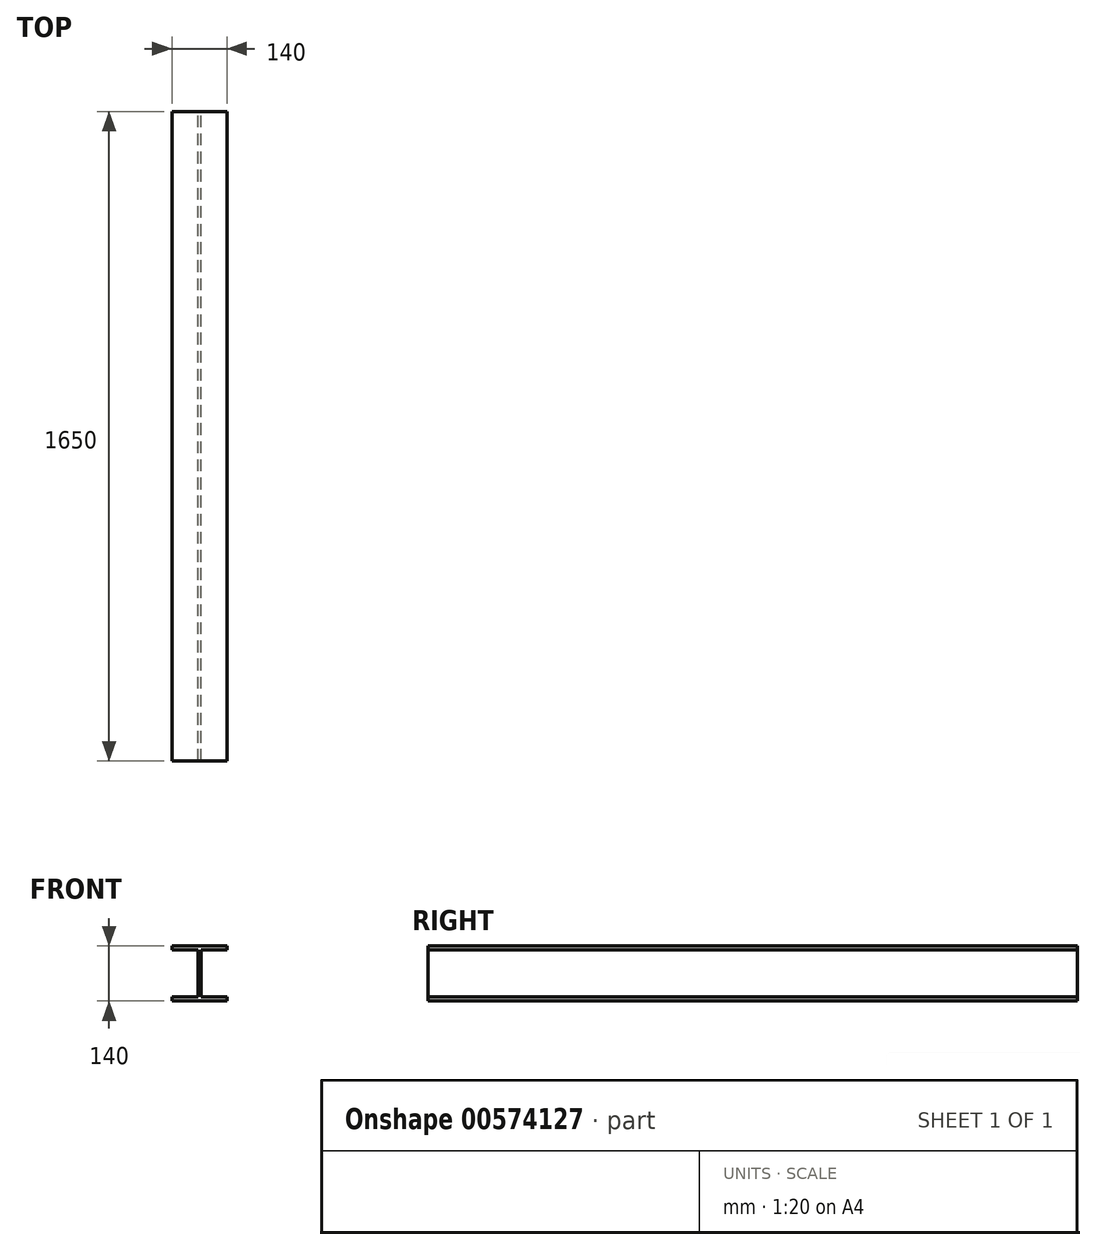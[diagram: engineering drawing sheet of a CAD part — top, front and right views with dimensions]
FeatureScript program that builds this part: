
annotation { "Feature Type Name" : "Feature", "Feature Type Description" : "" }
export const myFeature = defineFeature(function(context is Context, id is Id, definition is map)
    precondition{}
    {
        {
            var Q0;
            Q0=qCreatedBy(makeId("Front.planeOp"),FACE);
            var sketch = newSketch(context, id + "F0", { "sketchPlane" : qUnion([Q0])});
            skLineSegment(sketch, "E0", {"start": v(-70, 70) * mm, "end": v(70, 70) * mm});
            skLineSegment(sketch, "E1", {"start": v(-70, 70) * mm, "end": v(-70, 60) * mm});
            skLineSegment(sketch, "E2", {"start": v(-70, 60) * mm, "end": v(-4, 60) * mm});
            skLineSegment(sketch, "E3", {"start": v(-4, 60) * mm, "end": v(-4, -60) * mm});
            skLineSegment(sketch, "E4", {"start": v(-4, -60) * mm, "end": v(-70, -60) * mm});
            skLineSegment(sketch, "E5", {"start": v(-70, -60) * mm, "end": v(-70, -70) * mm});
            skLineSegment(sketch, "E6", {"start": v(-70, -70) * mm, "end": v(70, -70) * mm});
            skLineSegment(sketch, "E7", {"start": v(70, -70) * mm, "end": v(70, -60) * mm});
            skLineSegment(sketch, "E8", {"start": v(70, -60) * mm, "end": v(4, -60) * mm});
            skLineSegment(sketch, "E9", {"start": v(4, -60) * mm, "end": v(4, 60) * mm});
            skLineSegment(sketch, "E10", {"start": v(4, 60) * mm, "end": v(70, 60) * mm});
            skLineSegment(sketch, "E11", {"start": v(70, 60) * mm, "end": v(70, 70) * mm});
            skSolve(sketch);
        }
        {
            var Q0;
            Q0=makeQuery(id+"F0.imprint","IMPRINT",FACE,{"disambiguationData":[TD([[makeQuery(id+"F0.imprint","IMPRINT",EDGE,{"derivedFrom":sQuery(id+"F0.wireOp",EDGE,"E0")}),-1.0]])]});
            extrude(context, id + "F1", {"entities" : qUnion([Q0]), "endBound" : BoundingType.SYMMETRIC, "depth" : 1650 * mm, "offsetDistance" : 25 * mm});
        }
    });
